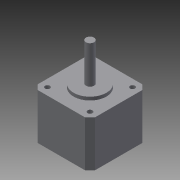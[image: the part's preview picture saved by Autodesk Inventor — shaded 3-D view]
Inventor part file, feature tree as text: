
AUTODESK INVENTOR PART (.ipt)
format: ipt  version: 2013 SP2 (Build 170200200, 200)  size: 112,640 bytes
history: native  units: mm
features: extrude x3, sketch x3, chamfer x1
ambient origin geometry x8: Origin, YZ Plane, XZ Plane, XY Plane, X Axis, Y Axis, Z Axis, Center Point
bodies: Solid1 (feature_tree)
feature tree (7):
  extrude  "Extrusion1"  Depth=35.0mm
  chamfer  "Chamfer1"  Distance=3.0mm
  sketch  "Sketch2"  dims[d2=26.0mm]
  extrude  "Extrusion2"  Depth=3.0mm
  extrude  "Extrusion3"  Depth=3.0mm
  sketch  "Sketch1"  dims[d0=35.0mm d1=35.0mm]
  sketch  "Sketch3"  dims[d3=3.0mm d4=3.0mm d5=3.0mm d6=3.0mm d7=28.0mm d8=0.0mm d9=5.0mm d10=3.0mm d11=2.0mm d12=45.0deg d13=20.0mm d14=25.0mm d15=0.0mm d16=2.0mm d17=0.0mm]
